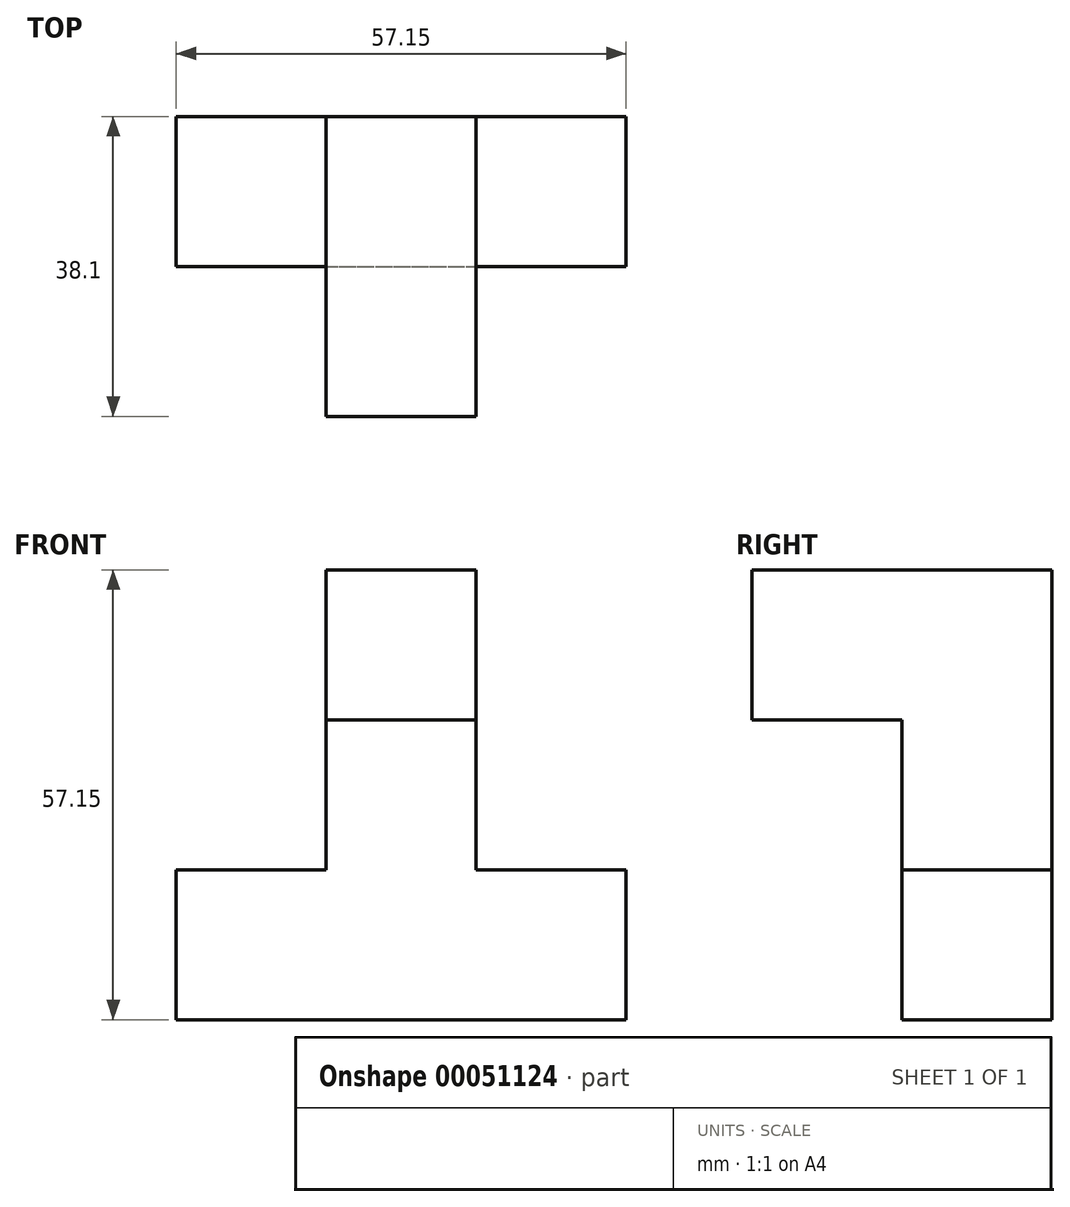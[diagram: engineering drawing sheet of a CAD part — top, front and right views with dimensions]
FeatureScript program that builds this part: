
annotation { "Feature Type Name" : "Feature", "Feature Type Description" : "" }
export const myFeature = defineFeature(function(context is Context, id is Id, definition is map)
    precondition{}
    {
        {
            var Q0;
            Q0=qCreatedBy(makeId("Top.planeOp"),FACE);
            var sketch = newSketch(context, id + "F0", { "sketchPlane" : qUnion([Q0])});
            skLineSegment(sketch, "E0.bottom", {"start": v(-19.5, -25.46) * mm, "end": v(37.65, -25.46) * mm});
            skLineSegment(sketch, "E0.top", {"start": v(-19.5, -6.41) * mm, "end": v(37.65, -6.41) * mm});
            skLineSegment(sketch, "E0.left", {"start": v(-19.5, -25.46) * mm, "end": v(-19.5, -6.41) * mm});
            skLineSegment(sketch, "E0.right", {"start": v(37.65, -25.46) * mm, "end": v(37.65, -6.41) * mm});
            skSolve(sketch);
        }
        {
            var Q0;
            Q0 = qSketchRegion(id + "F0", true);
            extrude(context, id + "F1", {"entities" : qUnion([Q0]), "depth" : 19.05 * mm});
        }
        {
            var Q0;
            Q0=makeQuery(id+"F1.opExtrude","CAP_FACE",FACE,{"disambiguationData":[OSD([sQuery(id+"F0.wireOp",EDGE,"E0.bottom"),sQuery(id+"F0.wireOp",EDGE,"E0.top"),sQuery(id+"F0.wireOp",EDGE,"E0.left"),sQuery(id+"F0.wireOp",EDGE,"E0.right")])],"isStart":false});
            var sketch = newSketch(context, id + "F2", { "sketchPlane" : qUnion([Q0])});
            skLineSegment(sketch, "E1.bottom", {"start": v(-19.5, -25.46) * mm, "end": v(-0.45, -25.46) * mm});
            skLineSegment(sketch, "E1.top", {"start": v(-19.5, -6.41) * mm, "end": v(-0.45, -6.41) * mm});
            skLineSegment(sketch, "E1.left", {"start": v(-19.5, -25.46) * mm, "end": v(-19.5, -6.41) * mm});
            skLineSegment(sketch, "E1.right", {"start": v(-0.45, -25.46) * mm, "end": v(-0.45, -6.41) * mm});
            skLineSegment(sketch, "E2.bottom", {"start": v(-0.45, -6.41) * mm, "end": v(18.6, -6.41) * mm});
            skLineSegment(sketch, "E2.top", {"start": v(-0.45, -25.46) * mm, "end": v(18.6, -25.46) * mm});
            skLineSegment(sketch, "E2.left", {"start": v(-0.45, -6.41) * mm, "end": v(-0.45, -25.46) * mm});
            skLineSegment(sketch, "E2.right", {"start": v(18.6, -6.41) * mm, "end": v(18.6, -25.46) * mm});
            skSolve(sketch);
        }
        {
            var Q0;
            Q0=makeQuery(id+"F2.imprint","IMPRINT",FACE,{"disambiguationData":[TD([[makeQuery(id+"F2.imprint","IMPRINT",EDGE,{"derivedFrom":sQuery(id+"F2.wireOp",EDGE,"E2.bottom")}),-1.0]])]});
            extrude(context, id + "F3", {"entities" : qUnion([Q0]), "operationType" : NewBodyOperationType.ADD, "depth" : 19.05 * mm});
        }
        {
            var Q0;
            Q0=makeQuery(id+"F3.opExtrude","CAP_FACE",FACE,{"disambiguationData":[OSD([sQuery(id+"F2.wireOp",EDGE,"E2.bottom"),sQuery(id+"F2.wireOp",EDGE,"E2.top"),sQuery(id+"F2.wireOp",EDGE,"E2.left"),sQuery(id+"F2.wireOp",EDGE,"E2.right")])],"isStart":false});
            var sketch = newSketch(context, id + "F4", { "sketchPlane" : qUnion([Q0])});
            skLineSegment(sketch, "E3.bottom", {"start": v(-0.45, -6.41) * mm, "end": v(18.6, -6.41) * mm});
            skLineSegment(sketch, "E3.top", {"start": v(-0.45, -44.51) * mm, "end": v(18.6, -44.51) * mm});
            skLineSegment(sketch, "E3.left", {"start": v(-0.45, -6.41) * mm, "end": v(-0.45, -44.51) * mm});
            skLineSegment(sketch, "E3.right", {"start": v(18.6, -6.41) * mm, "end": v(18.6, -44.51) * mm});
            skSolve(sketch);
        }
        {
            var Q0;
            Q0 = qSketchRegion(id + "F4", true);
            extrude(context, id + "F5", {"entities" : qUnion([Q0]), "operationType" : NewBodyOperationType.ADD, "depth" : 19.05 * mm});
        }
    });
